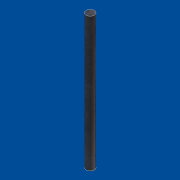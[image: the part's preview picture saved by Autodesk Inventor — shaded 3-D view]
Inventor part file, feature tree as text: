
AUTODESK INVENTOR PART (.ipt)
format: ipt  version: unknown  size: 148,992 bytes
history: native  units: mm
features: extrude x1, sketch x1
ambient origin geometry x8: Origin, YZ Plane, XZ Plane, XY Plane, X Axis, Y Axis, Z Axis, Center Point
feature tree (2):
  extrude  "Extrusion1"  Depth=32.0mm TaperAngle=0.0deg
  sketch  "Sketch1"  dims[d0=2.0mm d1=32.0mm d2=0.0mm]
